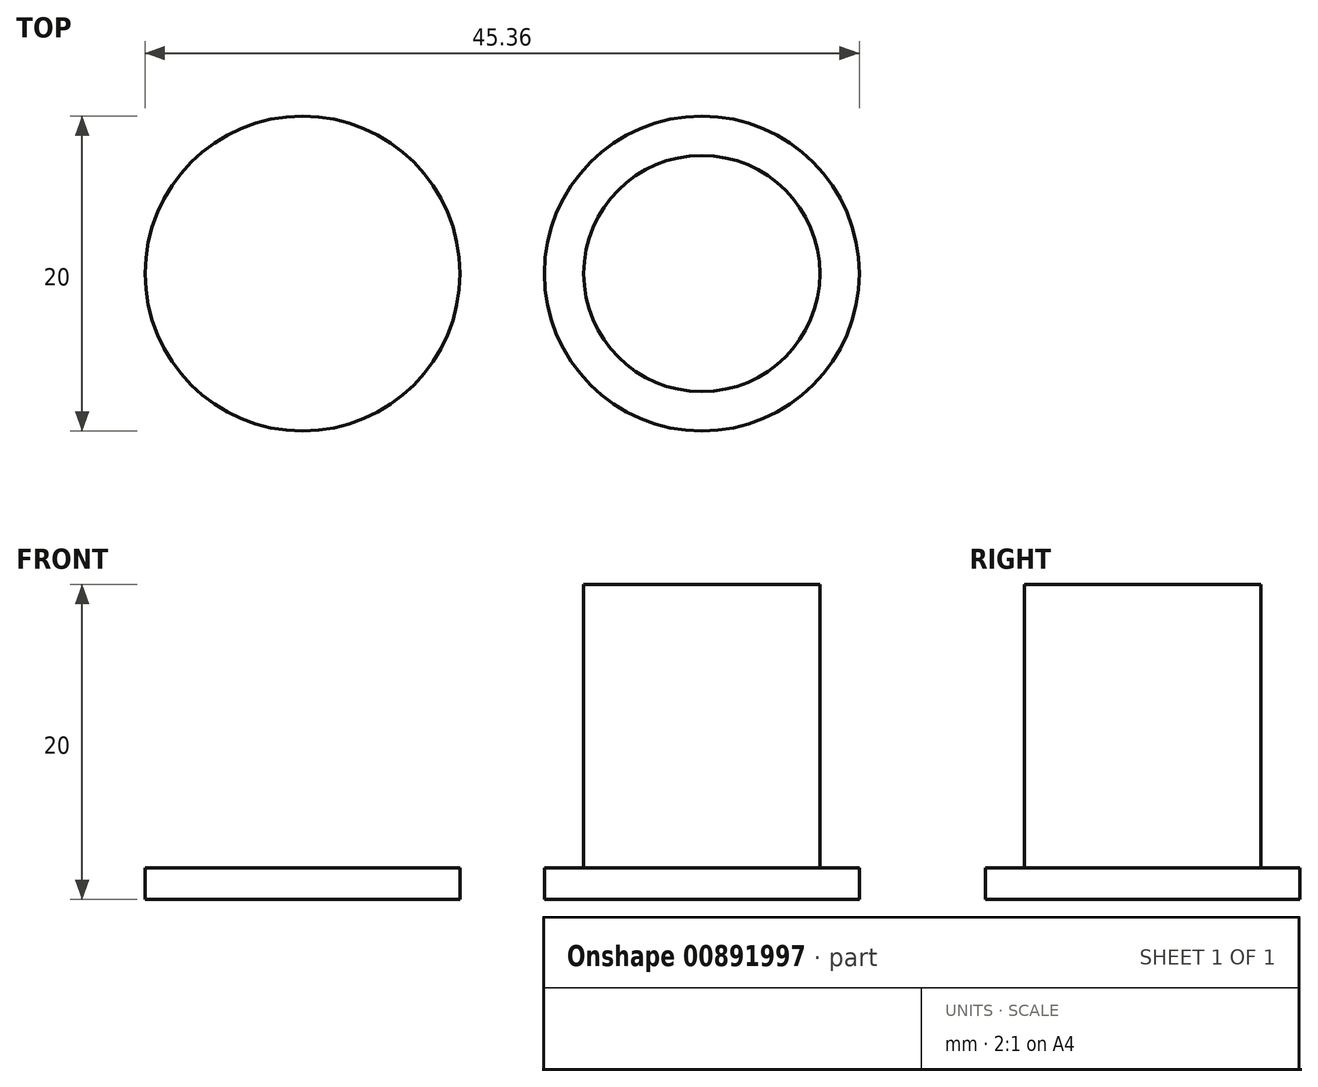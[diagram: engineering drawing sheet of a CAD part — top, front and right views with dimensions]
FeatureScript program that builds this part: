
annotation { "Feature Type Name" : "Feature", "Feature Type Description" : "" }
export const myFeature = defineFeature(function(context is Context, id is Id, definition is map)
    precondition{}
    {
        {
            var Q0;
            Q0=qCreatedBy(makeId("Top.planeOp"),FACE);
            var sketch = newSketch(context, id + "F0", { "sketchPlane" : qUnion([Q0])});
            skCircle(sketch, "E0", {"center": v(-25.36, 0) * mm, "radius": 10 * mm});
            skCircle(sketch, "E1", {"center": v(0, 0) * mm, "radius": 10 * mm});
            skSolve(sketch);
        }
        {
            var Q0;
            Q0=makeQuery(id+"F0.imprint","IMPRINT",FACE,{"disambiguationData":[TD([[makeQuery(id+"F0.imprint","IMPRINT",EDGE,{"derivedFrom":sQuery(id+"F0.wireOp",EDGE,"E1")}),1.0]])]});
            var Q1;
            Q1=makeQuery(id+"F0.imprint","IMPRINT",FACE,{"disambiguationData":[TD([[makeQuery(id+"F0.imprint","IMPRINT",EDGE,{"derivedFrom":sQuery(id+"F0.wireOp",EDGE,"E0")}),1.0]])]});
            extrude(context, id + "F1", {"entities" : qUnion([Q0, Q1]), "depth" : 2 * mm, "offsetDistance" : 25 * mm});
        }
        {
            var Q0;
            Q0=qCreatedBy(makeId("Top.planeOp"),FACE);
            var sketch = newSketch(context, id + "F2", { "sketchPlane" : qUnion([Q0])});
            skCircle(sketch, "E2", {"center": v(0, 0) * mm, "radius": 7.5 * mm});
            skSolve(sketch);
        }
        {
            var Q0;
            Q0 = qSketchRegion(id + "F2", true);
            extrude(context, id + "F3", {"entities" : qUnion([Q0]), "operationType" : NewBodyOperationType.ADD, "depth" : 20 * mm, "offsetDistance" : 25 * mm});
        }
        {
            var Q0;
            Q0=qCreatedBy(makeId("Top.planeOp"),FACE);
            var sketch = newSketch(context, id + "F4", { "sketchPlane" : qUnion([Q0])});
            skCircle(sketch, "E3", {"center": v(32.6, 0) * mm, "radius": 8.5 * mm});
            skSolve(sketch);
        }
        {
            var Q0;
            Q0=sQuery(id+"F4.wireOp",EDGE,"E3");
            extrude(context, id + "F5", {"bodyType" : ToolBodyType.SURFACE, "surfaceEntities" : qUnion([Q0]), "depth" : 5 * mm, "offsetDistance" : 25 * mm});
        }
    });
